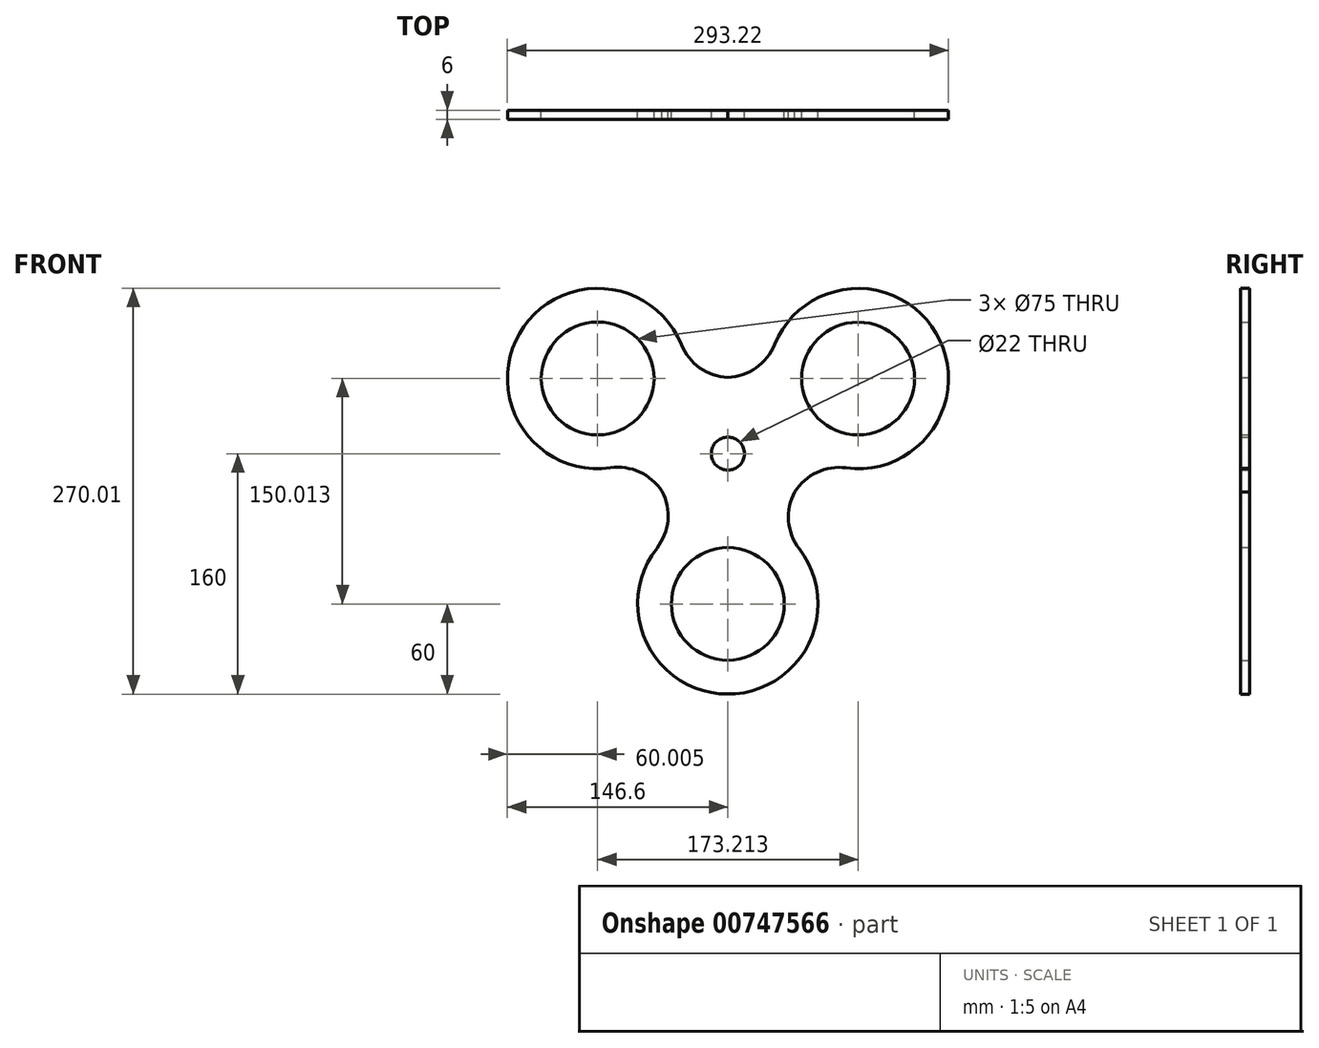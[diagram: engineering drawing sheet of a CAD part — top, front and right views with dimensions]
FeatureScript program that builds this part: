
annotation { "Feature Type Name" : "Feature", "Feature Type Description" : "" }
export const myFeature = defineFeature(function(context is Context, id is Id, definition is map)
    precondition{}
    {
        {
            var Q0;
            Q0=qCreatedBy(makeId("Front.planeOp"),FACE);
            var sketch = newSketch(context, id + "F0", { "sketchPlane" : qUnion([Q0])});
            skCircle(sketch, "E0", {"center": v(0, 0) * mm, "radius": 11 * mm});
            skCircle(sketch, "E1", {"center": v(86.62, 49.97) * mm, "radius": 60 * mm});
            skCircle(sketch, "E2", {"center": v(0, -100) * mm, "radius": 60 * mm});
            skCircle(sketch, "E3", {"center": v(-86.6, 50.01) * mm, "radius": 60 * mm});
            skCircle(sketch, "E4", {"center": v(-86.6, 50.01) * mm, "radius": 37.5 * mm});
            skCircle(sketch, "E5", {"center": v(86.62, 49.97) * mm, "radius": 37.5 * mm});
            skCircle(sketch, "E6", {"center": v(0, -100) * mm, "radius": 37.5 * mm});
            skLineSegment(sketch, "E7", {"start": v(30.91, -48.57) * mm, "end": v(57.86, -2.69) * mm});
            skLineSegment(sketch, "E8", {"start": v(26.62, 50.74) * mm, "end": v(-26.6, 50.74) * mm});
            skLineSegment(sketch, "E9", {"start": v(-30.2, -48.15) * mm, "end": v(-57.14, -2.26) * mm});
            skSolve(sketch);
        }
        {
            var Q0;
            Q0=makeQuery(id+"F0.imprint","IMPRINT",FACE,{"disambiguationData":[TD([[makeQuery(id+"F0.imprint","IMPRINT",EDGE,{"derivedFrom":sQuery(id+"F0.wireOp",EDGE,"E5")}),-1.0]])]});
            var Q1;
            Q1=makeQuery(id+"F0.imprint","IMPRINT",FACE,{"disambiguationData":[TD([[makeQuery(id+"F0.imprint","IMPRINT",EDGE,{"derivedFrom":sQuery(id+"F0.wireOp",EDGE,"E3")}),1.0]])]});
            var Q2;
            Q2=makeQuery(id+"F0.imprint","IMPRINT",FACE,{"disambiguationData":[TD([[makeQuery(id+"F0.imprint","IMPRINT",EDGE,{"derivedFrom":sQuery(id+"F0.wireOp",EDGE,"E0")}),-1.0]])]});
            var Q3;
            Q3=makeQuery(id+"F0.imprint","IMPRINT",FACE,{"disambiguationData":[TD([[makeQuery(id+"F0.imprint","IMPRINT",EDGE,{"derivedFrom":sQuery(id+"F0.wireOp",EDGE,"E6")}),-1.0]])]});
            extrude(context, id + "F1", {"entities" : qUnion([Q0, Q1, Q2, Q3]), "depth" : 6 * mm, "offsetDistance" : 25 * mm});
        }
        {
            var Q0;
            Q0=makeQuery(id+"F1.opExtrude","SWEPT_EDGE",EDGE,{"disambiguationData":[OSD([sQuery(id+"F0.wireOp",EDGE,"E2"),sQuery(id+"F0.wireOp",EDGE,"E9")])]});
            var Q1;
            Q1=makeQuery(id+"F1.opExtrude","SWEPT_EDGE",EDGE,{"disambiguationData":[OSD([sQuery(id+"F0.wireOp",EDGE,"E1"),sQuery(id+"F0.wireOp",EDGE,"E8")])]});
            var Q2;
            Q2=makeQuery(id+"F1.opExtrude","SWEPT_EDGE",EDGE,{"disambiguationData":[OSD([sQuery(id+"F0.wireOp",EDGE,"E3"),sQuery(id+"F0.wireOp",EDGE,"E8")])]});
            var Q3;
            Q3=makeQuery(id+"F1.opExtrude","SWEPT_EDGE",EDGE,{"disambiguationData":[OSD([sQuery(id+"F0.wireOp",EDGE,"E1"),sQuery(id+"F0.wireOp",EDGE,"E7")])]});
            var Q4;
            Q4=makeQuery(id+"F1.opExtrude","SWEPT_EDGE",EDGE,{"disambiguationData":[OSD([sQuery(id+"F0.wireOp",EDGE,"E2"),sQuery(id+"F0.wireOp",EDGE,"E7")])]});
            var Q5;
            Q5=makeQuery(id+"F1.opExtrude","SWEPT_EDGE",EDGE,{"disambiguationData":[OSD([sQuery(id+"F0.wireOp",EDGE,"E3"),sQuery(id+"F0.wireOp",EDGE,"E9")])]});
            fillet(context, id + "F2", {"entities" : qUnion([Q0, Q1, Q2, Q3, Q4, Q5]), "radius" : 35 * mm, "tangentPropagation" : true, "allowEdgeOverflow" : false});
        }
    });
